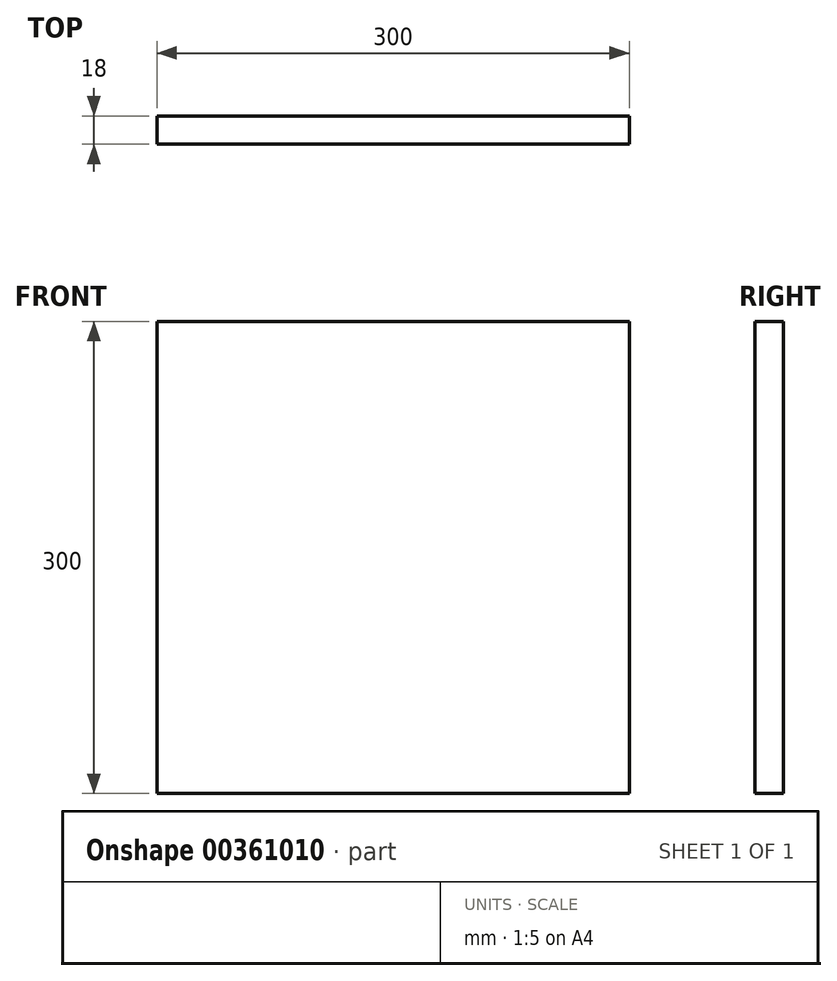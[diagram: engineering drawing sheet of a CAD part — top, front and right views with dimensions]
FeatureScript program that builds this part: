
annotation { "Feature Type Name" : "Feature", "Feature Type Description" : "" }
export const myFeature = defineFeature(function(context is Context, id is Id, definition is map)
    precondition{}
    {
        {
            var Q0;
            Q0=qCreatedBy(makeId("Top.planeOp"),FACE);
            var sketch = newSketch(context, id + "F0", { "sketchPlane" : qUnion([Q0])});
            skLineSegment(sketch, "E0.bottom", {"start": v(0, 0) * mm, "end": v(2600, 0) * mm, "construction": true});
            skLineSegment(sketch, "E0.top", {"start": v(0, 1200) * mm, "end": v(2600, 1200) * mm, "construction": true});
            skLineSegment(sketch, "E0.left", {"start": v(0, 0) * mm, "end": v(0, 1200) * mm, "construction": true});
            skLineSegment(sketch, "E0.right", {"start": v(2600, 0) * mm, "end": v(2600, 1200) * mm, "construction": true});
            skLineSegment(sketch, "E1", {"start": v(300, 1200) * mm, "end": v(300, 0) * mm, "construction": true});
            skLineSegment(sketch, "E2", {"start": v(2461.96, 1200) * mm, "end": v(2461.96, 0) * mm, "construction": true});
            skLineSegment(sketch, "E3.bottom", {"start": v(300, 0) * mm, "end": v(2461.96, 0) * mm});
            skLineSegment(sketch, "E3.top", {"start": v(300, 1200) * mm, "end": v(2461.96, 1200) * mm});
            skLineSegment(sketch, "E3.left", {"start": v(300, 0) * mm, "end": v(300, 1200) * mm});
            skLineSegment(sketch, "E3.right", {"start": v(2461.96, 0) * mm, "end": v(2461.96, 1200) * mm});
            skLineSegment(sketch, "E4.top", {"start": v(300, 18) * mm, "end": v(2461.96, 18) * mm});
            skLineSegment(sketch, "E4.left", {"start": v(300, 0) * mm, "end": v(300, 18) * mm});
            skLineSegment(sketch, "E4.right", {"start": v(2461.96, 0) * mm, "end": v(2461.96, 18) * mm});
            skLineSegment(sketch, "E5.top", {"start": v(300, 1182) * mm, "end": v(2461.96, 1182) * mm});
            skLineSegment(sketch, "E5.left", {"start": v(300, 1200) * mm, "end": v(300, 1182) * mm});
            skLineSegment(sketch, "E5.right", {"start": v(2461.96, 1200) * mm, "end": v(2461.96, 1182) * mm});
            skLineSegment(sketch, "E6.bottom", {"start": v(300, 1182) * mm, "end": v(318, 1182) * mm});
            skLineSegment(sketch, "E6.top", {"start": v(300, 18) * mm, "end": v(318, 18) * mm});
            skLineSegment(sketch, "E6.left", {"start": v(300, 1182) * mm, "end": v(300, 18) * mm});
            skLineSegment(sketch, "E7.bottom", {"start": v(2461.96, 1182) * mm, "end": v(2443.96, 1182) * mm});
            skLineSegment(sketch, "E7.top", {"start": v(2461.96, 18) * mm, "end": v(2443.96, 18) * mm});
            skLineSegment(sketch, "E7.left", {"start": v(2461.96, 1182) * mm, "end": v(2461.96, 18) * mm});
            skLineSegment(sketch, "E7.right", {"start": v(2443.96, 1182) * mm, "end": v(2443.96, 18) * mm});
            skLineSegment(sketch, "E8.bottom", {"start": v(0, 0) * mm, "end": v(300, 0) * mm});
            skLineSegment(sketch, "E8.top", {"start": v(0, 18) * mm, "end": v(300, 18) * mm});
            skLineSegment(sketch, "E8.left", {"start": v(0, 0) * mm, "end": v(0, 18) * mm});
            skLineSegment(sketch, "E9.bottom", {"start": v(0, 1200) * mm, "end": v(300, 1200) * mm});
            skLineSegment(sketch, "E9.top", {"start": v(0, 1182) * mm, "end": v(300, 1182) * mm});
            skLineSegment(sketch, "E9.left", {"start": v(0, 1200) * mm, "end": v(0, 1182) * mm});
            skLineSegment(sketch, "E10.bottom", {"start": v(0, 1182) * mm, "end": v(18, 1182) * mm});
            skLineSegment(sketch, "E10.top", {"start": v(0, 18) * mm, "end": v(18, 18) * mm});
            skLineSegment(sketch, "E10.left", {"start": v(0, 1182) * mm, "end": v(0, 18) * mm});
            skLineSegment(sketch, "E10.right", {"start": v(18, 1182) * mm, "end": v(18, 18) * mm});
            skLineSegment(sketch, "E11.bottom", {"start": v(300, 1182) * mm, "end": v(282, 1182) * mm});
            skLineSegment(sketch, "E11.top", {"start": v(300, 18) * mm, "end": v(282, 18) * mm});
            skLineSegment(sketch, "E11.right", {"start": v(282, 1182) * mm, "end": v(282, 18) * mm});
            skLineSegment(sketch, "E12.bottom", {"start": v(2161.96, 1182) * mm, "end": v(2179.96, 1182) * mm});
            skLineSegment(sketch, "E12.top", {"start": v(2161.96, 18) * mm, "end": v(2179.96, 18) * mm});
            skLineSegment(sketch, "E12.left", {"start": v(2161.96, 1182) * mm, "end": v(2161.96, 18) * mm});
            skLineSegment(sketch, "E12.right", {"start": v(2179.96, 1182) * mm, "end": v(2179.96, 18) * mm});
            skSolve(sketch);
        }
        {
            var Q0;
            Q0=makeQuery(id+"F0.imprint","IMPRINT",FACE,{"disambiguationData":[TD([[makeQuery(id+"F0.imprint","IMPRINT",EDGE,{"derivedFrom":sQuery(id+"F0.wireOp",EDGE,"E8.bottom")}),1.0]])]});
            extrude(context, id + "F1", {"entities" : qUnion([Q0]), "depth" : 300 * mm});
        }
    });
